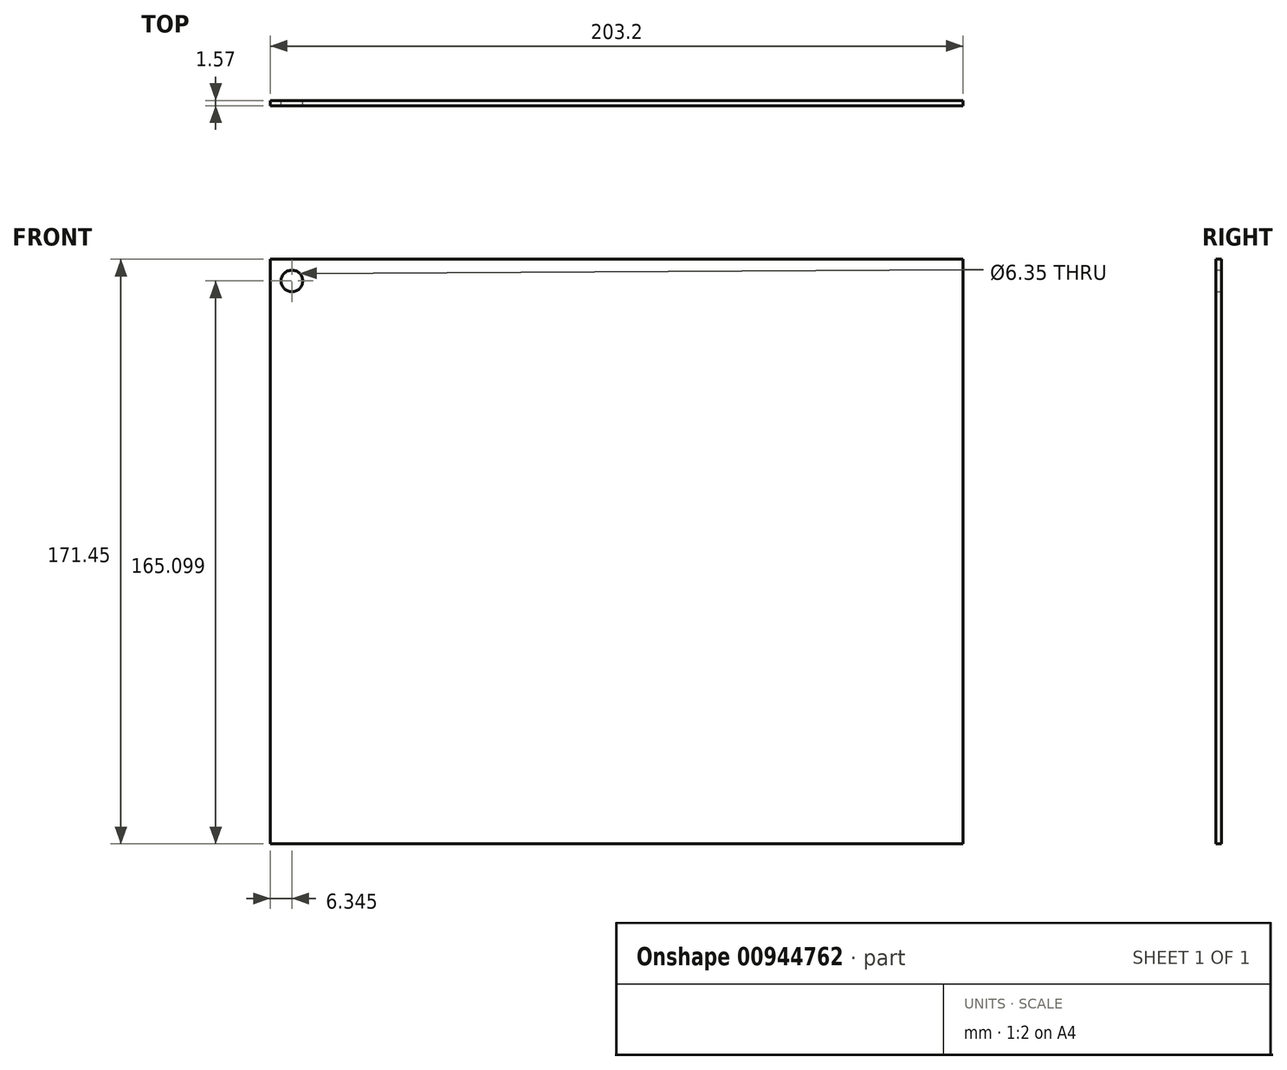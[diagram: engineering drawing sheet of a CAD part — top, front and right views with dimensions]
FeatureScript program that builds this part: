
annotation { "Feature Type Name" : "Feature", "Feature Type Description" : "" }
export const myFeature = defineFeature(function(context is Context, id is Id, definition is map)
    precondition{}
    {
        {
            var Q0;
            Q0=qCreatedBy(makeId("Front.planeOp"),FACE);
            var sketch = newSketch(context, id + "F0", { "sketchPlane" : qUnion([Q0])});
            skLineSegment(sketch, "E0.bottom", {"start": v(101.05, -82.45) * mm, "end": v(-102.15, -82.45) * mm});
            skLineSegment(sketch, "E0.top", {"start": v(101.05, 89) * mm, "end": v(-102.15, 89) * mm});
            skLineSegment(sketch, "E0.left", {"start": v(101.05, -82.45) * mm, "end": v(101.05, 89) * mm});
            skLineSegment(sketch, "E0.right", {"start": v(-102.15, -82.45) * mm, "end": v(-102.15, 89) * mm});
            skPoint(sketch, "E0.middle", {"position": v(-0.55, 3.27) * mm});
            skCircle(sketch, "E1", {"center": v(-95.8, 82.65) * mm, "radius": 3.18 * mm});
            skSolve(sketch);
        }
        {
            var Q0;
            Q0=makeQuery(id+"F0.imprint","IMPRINT",FACE,{"disambiguationData":[TD([[makeQuery(id+"F0.imprint","IMPRINT",EDGE,{"derivedFrom":sQuery(id+"F0.wireOp",EDGE,"E0.bottom")}),-1.0]])]});
            extrude(context, id + "F1", {"entities" : qUnion([Q0]), "depth" : 1.57 * mm, "offsetDistance" : 25.4 * mm});
        }
    });
